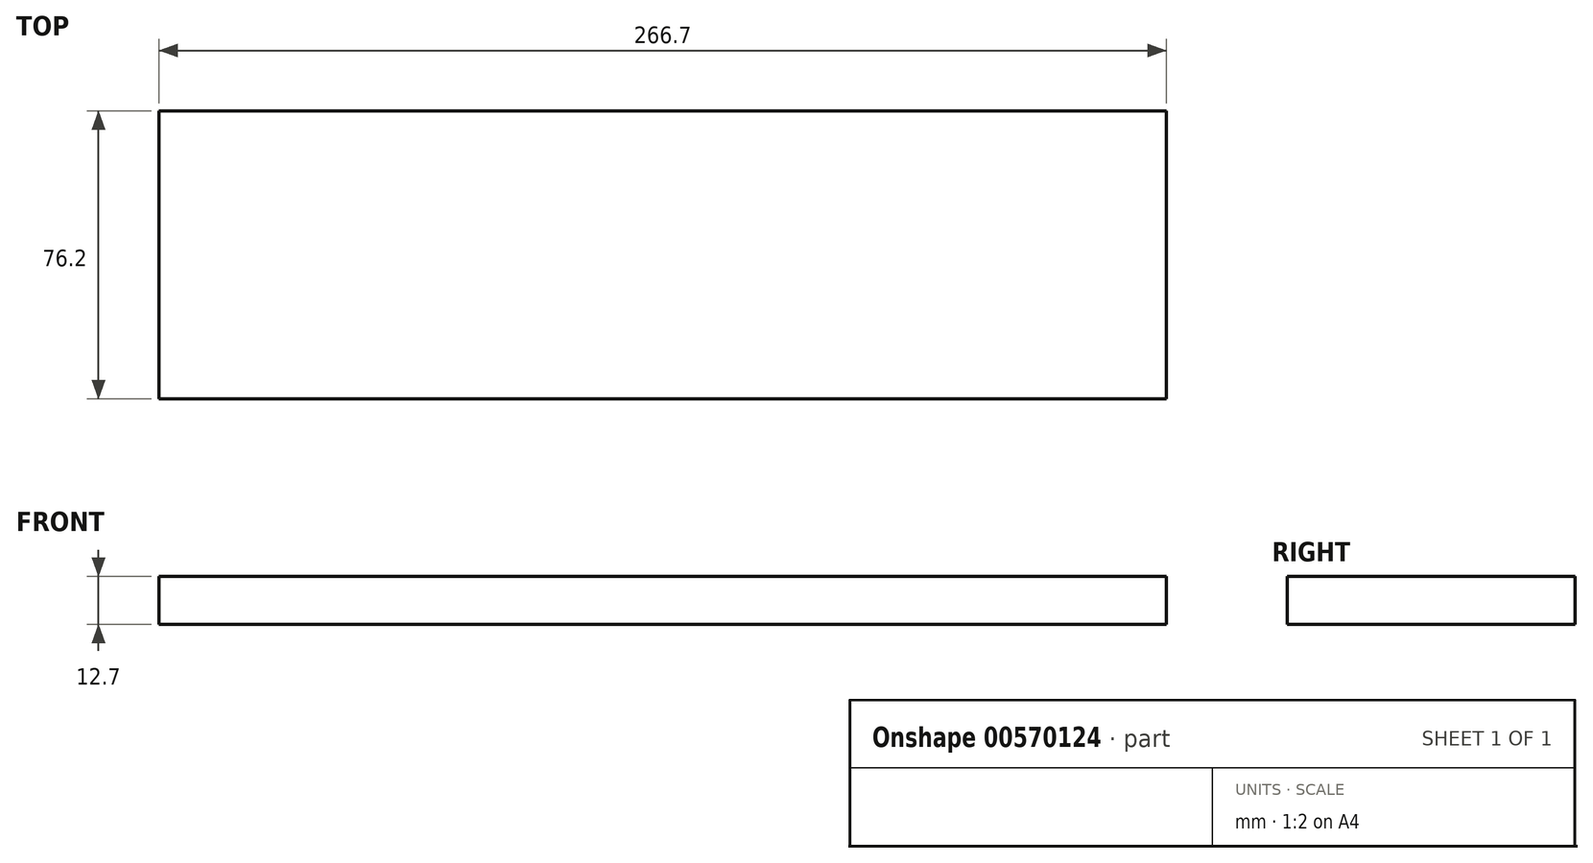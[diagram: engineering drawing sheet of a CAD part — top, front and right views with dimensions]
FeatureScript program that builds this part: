
annotation { "Feature Type Name" : "Feature", "Feature Type Description" : "" }
export const myFeature = defineFeature(function(context is Context, id is Id, definition is map)
    precondition{}
    {
        {
            var Q0;
            Q0=qCreatedBy(makeId("Front.planeOp"),FACE);
            var sketch = newSketch(context, id + "F0", { "sketchPlane" : qUnion([Q0])});
            skLineSegment(sketch, "E0.bottom", {"start": v(0, 0) * mm, "end": v(266.7, 0) * mm});
            skLineSegment(sketch, "E0.top", {"start": v(0, 12.7) * mm, "end": v(266.7, 12.7) * mm});
            skLineSegment(sketch, "E0.left", {"start": v(0, 0) * mm, "end": v(0, 12.7) * mm});
            skLineSegment(sketch, "E0.right", {"start": v(266.7, 0) * mm, "end": v(266.7, 12.7) * mm});
            skSolve(sketch);
        }
        {
            var Q0;
            Q0=makeQuery(id+"F0.imprint","IMPRINT",FACE,{"disambiguationData":[TD([[makeQuery(id+"F0.imprint","IMPRINT",EDGE,{"derivedFrom":sQuery(id+"F0.wireOp",EDGE,"E0.bottom")}),1.0]])]});
            extrude(context, id + "F1", {"entities" : qUnion([Q0]), "endBound" : BoundingType.SYMMETRIC, "depth" : 76.2 * mm, "offsetDistance" : 25.4 * mm});
        }
    });
